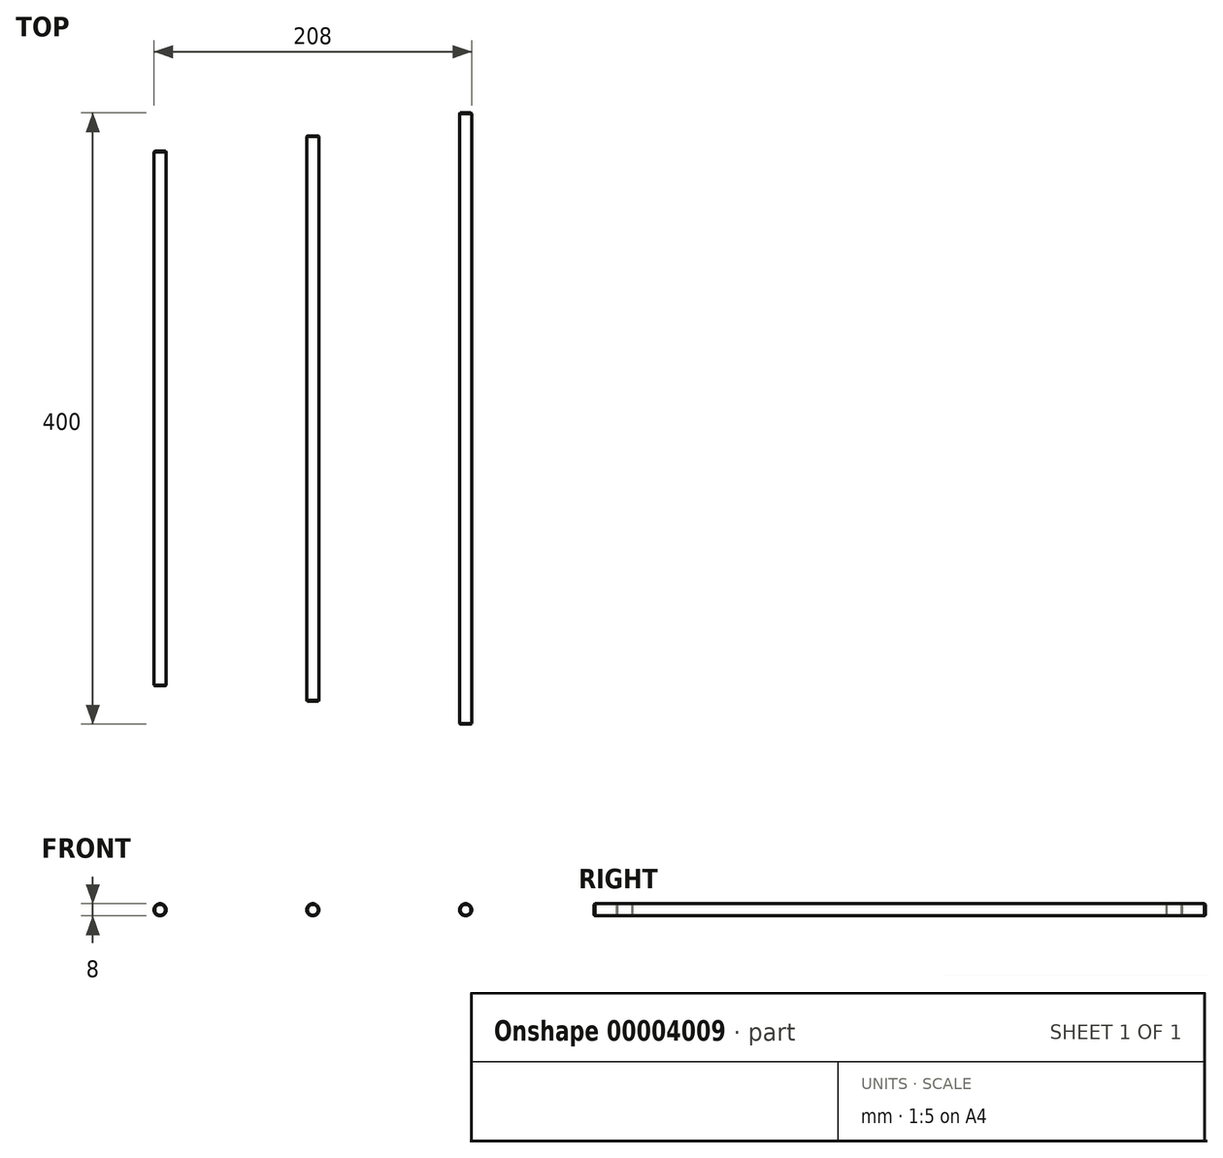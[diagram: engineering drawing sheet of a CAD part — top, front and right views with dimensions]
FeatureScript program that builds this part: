
annotation { "Feature Type Name" : "Feature", "Feature Type Description" : "" }
export const myFeature = defineFeature(function(context is Context, id is Id, definition is map)
    precondition{}
    {
        {
            var Q0;
            Q0=qCreatedBy(makeId("Front.planeOp"),FACE);
            var sketch = newSketch(context, id + "F0", { "sketchPlane" : qUnion([Q0])});
            skCircle(sketch, "E0", {"center": v(0, 0) * mm, "radius": 4 * mm});
            skSolve(sketch);
        }
        {
            var Q0;
            Q0=makeQuery(id+"F0.imprint","IMPRINT",FACE,{"disambiguationData":[TD([[makeQuery(id+"F0.imprint","IMPRINT",EDGE,{"derivedFrom":sQuery(id+"F0.wireOp",EDGE,"E0")}),1.0]])]});
            extrude(context, id + "F1", {"entities" : qUnion([Q0]), "depth" : 400 * mm, "symmetric" : true});
        }
        {
            var Q0;
            Q0=makeQuery(id+"F1.opExtrude","CAP_EDGE",EDGE,{"disambiguationData":[OSD([sQuery(id+"F0.wireOp",EDGE,"E0")])],"isStart":false});
            var Q1;
            Q1=makeQuery(id+"F1.opExtrude","CAP_EDGE",EDGE,{"disambiguationData":[OSD([sQuery(id+"F0.wireOp",EDGE,"E0")])],"isStart":true});
            chamfer(context, id + "F2", {"entities" : qUnion([Q0, Q1]), "width" : .5 * mm, "tangentPropagation" : true});
        }
        {
            var Q0;
            Q0=makeQuery(id+"F1.opExtrude","SWEPT_BODY",BODY,{"disambiguationData":[OSD([sQuery(id+"F0.wireOp",EDGE,"E0")])]});
            transform(context, id + "F3", {"entities" : qUnion([Q0]), "transformType" : TransformType.TRANSLATION_3D, "dx" : 200 * mm, "dy" : 0 * mm, "dz" : 0 * mm, "makeCopy" : false});
        }
        {
            var Q0;
            Q0=makeQuery(id+"F0.imprint","IMPRINT",FACE,{"disambiguationData":[TD([[makeQuery(id+"F0.imprint","IMPRINT",EDGE,{"derivedFrom":sQuery(id+"F0.wireOp",EDGE,"E0")}),1.0]])]});
            extrude(context, id + "F4", {"entities" : qUnion([Q0]), "depth" : 370 * mm, "symmetric" : true});
        }
        {
            var Q0;
            Q0=makeQuery(id+"F4.opExtrude","CAP_EDGE",EDGE,{"disambiguationData":[OSD([sQuery(id+"F0.wireOp",EDGE,"E0")])],"isStart":false});
            var Q1;
            Q1=makeQuery(id+"F4.opExtrude","CAP_EDGE",EDGE,{"disambiguationData":[OSD([sQuery(id+"F0.wireOp",EDGE,"E0")])],"isStart":true});
            chamfer(context, id + "F5", {"entities" : qUnion([Q0, Q1]), "width" : .5 * mm, "tangentPropagation" : true});
        }
        {
            var Q0;
            Q0=makeQuery(id+"F4.opExtrude","SWEPT_BODY",BODY,{"disambiguationData":[OSD([sQuery(id+"F0.wireOp",EDGE,"E0")])]});
            transform(context, id + "F6", {"entities" : qUnion([Q0]), "transformType" : TransformType.TRANSLATION_3D, "dx" : 100 * mm, "dy" : 0 * mm, "dz" : 0 * mm, "makeCopy" : false});
        }
        {
            var Q0;
            Q0=makeQuery(id+"F0.imprint","IMPRINT",FACE,{"disambiguationData":[TD([[makeQuery(id+"F0.imprint","IMPRINT",EDGE,{"derivedFrom":sQuery(id+"F0.wireOp",EDGE,"E0")}),1.0]])]});
            extrude(context, id + "F7", {"entities" : qUnion([Q0]), "depth" : 350 * mm, "symmetric" : true});
        }
        {
            var Q0;
            Q0=makeQuery(id+"F7.opExtrude","CAP_EDGE",EDGE,{"disambiguationData":[OSD([sQuery(id+"F0.wireOp",EDGE,"E0")])],"isStart":false});
            var Q1;
            Q1=makeQuery(id+"F7.opExtrude","CAP_EDGE",EDGE,{"disambiguationData":[OSD([sQuery(id+"F0.wireOp",EDGE,"E0")])],"isStart":true});
            chamfer(context, id + "F8", {"entities" : qUnion([Q0, Q1]), "width" : .5 * mm, "tangentPropagation" : true});
        }
    });
